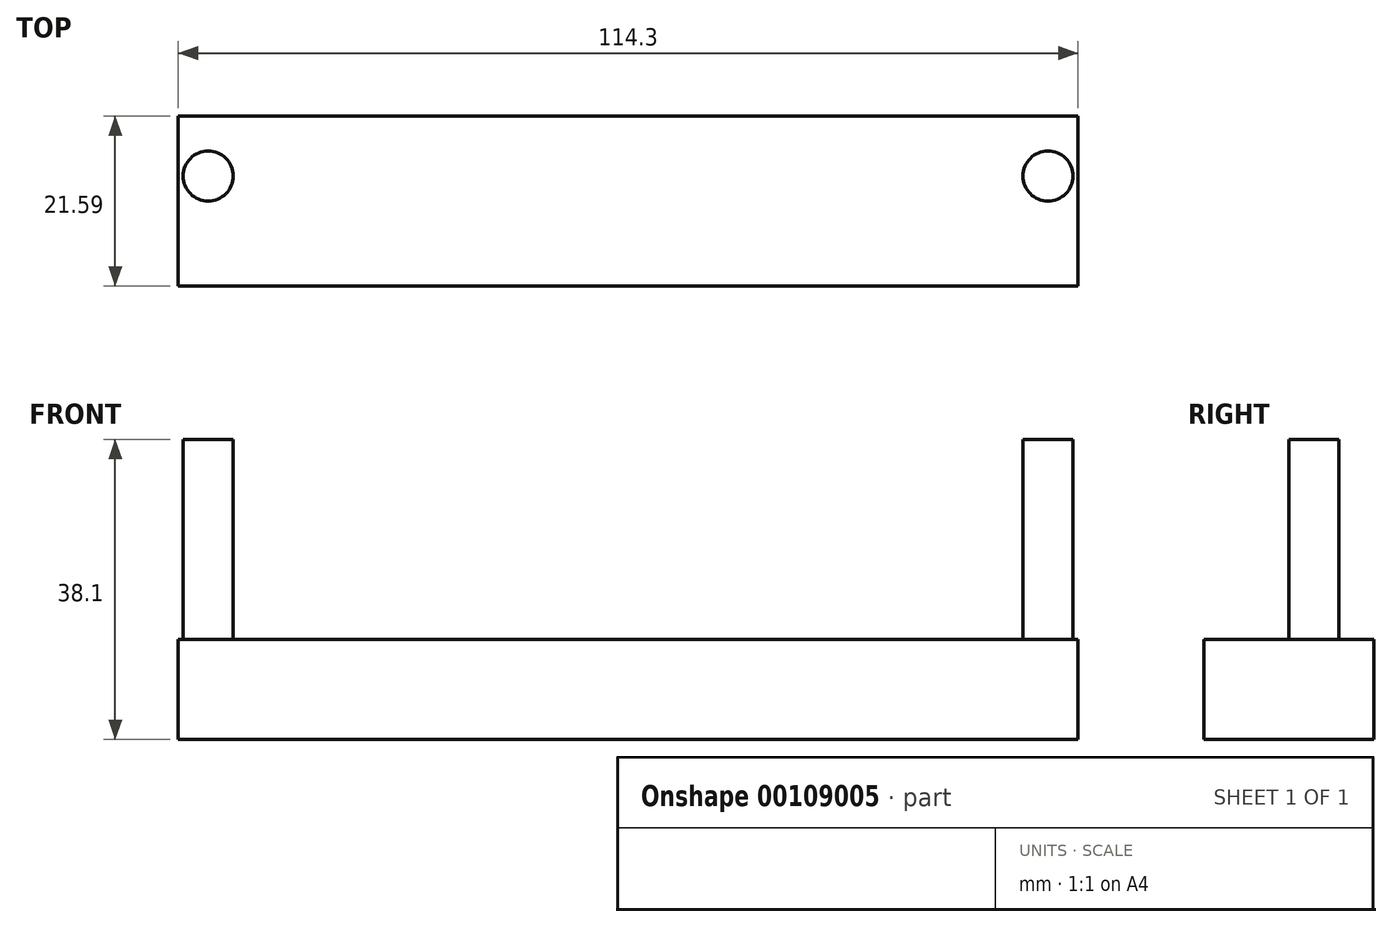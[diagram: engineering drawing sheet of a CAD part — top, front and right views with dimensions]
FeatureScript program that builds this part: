
annotation { "Feature Type Name" : "Feature", "Feature Type Description" : "" }
export const myFeature = defineFeature(function(context is Context, id is Id, definition is map)
    precondition{}
    {
        {
            var Q0;
            Q0=qCreatedBy(makeId("Front.planeOp"),FACE);
            var sketch = newSketch(context, id + "F0", { "sketchPlane" : qUnion([Q0])});
            skLineSegment(sketch, "E0", {"start": v(0, 0) * mm, "end": v(0, 12.7) * mm});
            skLineSegment(sketch, "E1", {"start": v(0, 0) * mm, "end": v(114.3, 0) * mm});
            skLineSegment(sketch, "E2", {"start": v(0, 12.7) * mm, "end": v(114.3, 12.7) * mm});
            skLineSegment(sketch, "E3", {"start": v(114.3, 12.7) * mm, "end": v(114.3, 0) * mm});
            skSolve(sketch);
        }
        {
            var Q0;
            Q0=makeQuery(id+"F0.imprint","IMPRINT",FACE,{"disambiguationData":[TD([[makeQuery(id+"F0.imprint","IMPRINT",EDGE,{"derivedFrom":sQuery(id+"F0.wireOp",EDGE,"E0")}),-1.0]])]});
            extrude(context, id + "F1", {"entities" : qUnion([Q0]), "depth" : 21.59 * mm});
        }
        {
            var Q0;
            Q0=makeQuery(id+"F1.opExtrude","SWEPT_FACE",FACE,{"disambiguationData":[OSD([sQuery(id+"F0.wireOp",EDGE,"E2")])]});
            var sketch = newSketch(context, id + "F2", { "sketchPlane" : qUnion([Q0])});
            skLineSegment(sketch, "E4", {"start": v(0, 0) * mm, "end": v(0, -7.62) * mm});
            skLineSegment(sketch, "E5", {"start": v(0, -7.62) * mm, "end": v(3.81, -7.62) * mm});
            skCircle(sketch, "E6", {"center": v(3.81, -7.62) * mm, "radius": 3.18 * mm});
            skLineSegment(sketch, "E7", {"start": v(0, 0) * mm, "end": v(114.3, 0) * mm});
            skLineSegment(sketch, "E8", {"start": v(114.3, 0) * mm, "end": v(114.3, -7.62) * mm});
            skLineSegment(sketch, "E9", {"start": v(114.3, -7.62) * mm, "end": v(110.5, -7.62) * mm});
            skCircle(sketch, "E10", {"center": v(110.5, -7.62) * mm, "radius": 3.18 * mm});
            skSolve(sketch);
        }
        {
            var Q0;
            Q0=makeQuery(id+"F2.imprint","IMPRINT",FACE,{"disambiguationData":[TD([[makeQuery(id+"F2.imprint","IMPRINT",EDGE,{"derivedFrom":sQuery(id+"F2.wireOp",EDGE,"E6")}),1.0]])]});
            extrude(context, id + "F3", {"entities" : qUnion([Q0]), "operationType" : NewBodyOperationType.ADD, "depth" : 25.4 * mm});
        }
        {
            var Q0;
            Q0=makeQuery(id+"F2.imprint","IMPRINT",FACE,{"disambiguationData":[TD([[makeQuery(id+"F2.imprint","IMPRINT",EDGE,{"derivedFrom":sQuery(id+"F2.wireOp",EDGE,"E10")}),1.0]])]});
            extrude(context, id + "F4", {"entities" : qUnion([Q0]), "operationType" : NewBodyOperationType.ADD, "depth" : 25.4 * mm});
        }
    });
